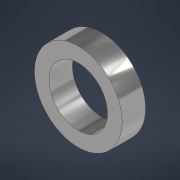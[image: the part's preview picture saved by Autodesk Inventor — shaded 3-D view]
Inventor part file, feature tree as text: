
AUTODESK INVENTOR PART (.ipt)
format: ipt  version: 2021 (Build 250183000, 183)  size: 100,352 bytes
history: native  units: mm
features: extrude x1, sketch x1
ambient origin geometry x8: Origin, YZ Plane, XZ Plane, XY Plane, X Axis, Y Axis, Z Axis, Center Point
bodies: Volumenkörper1 (feature_tree)
feature tree (2):
  extrude  "Extrusion1"  Depth=4.0mm
  sketch  "Skizze1"  dims[d0=10.0mm d1=15.0mm d2=4.0mm d3=0.0mm]
